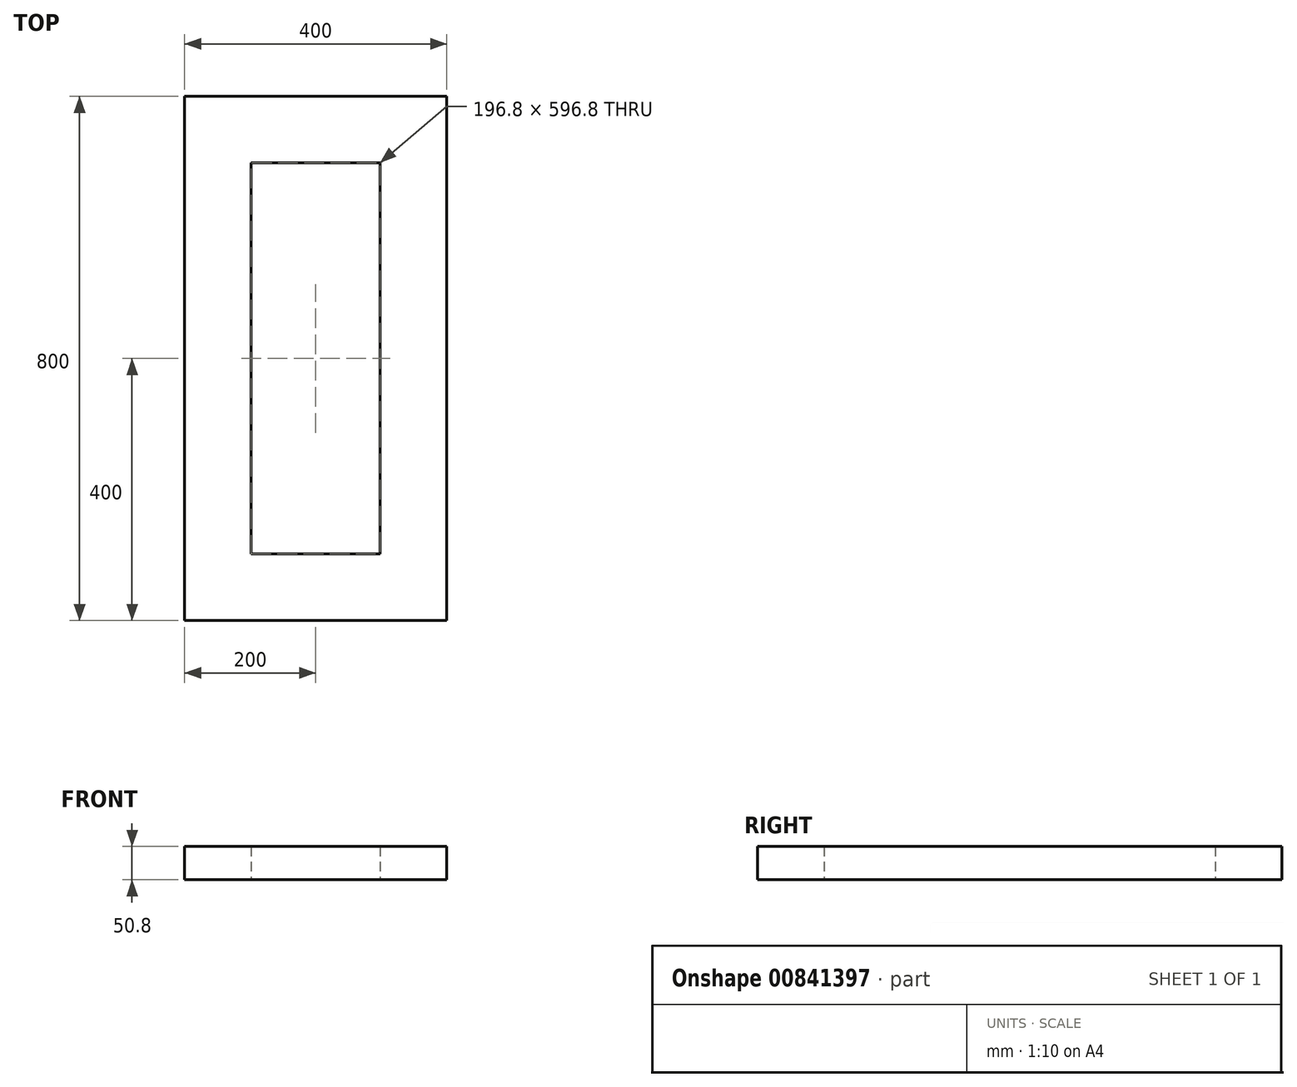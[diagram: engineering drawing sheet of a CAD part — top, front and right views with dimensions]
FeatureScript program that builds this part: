
annotation { "Feature Type Name" : "Feature", "Feature Type Description" : "" }
export const myFeature = defineFeature(function(context is Context, id is Id, definition is map)
    precondition{}
    {
        {
            var Q0;
            Q0=qCreatedBy(makeId("Top.planeOp"),FACE);
            var sketch = newSketch(context, id + "F0", { "sketchPlane" : qUnion([Q0])});
            skLineSegment(sketch, "E0.bottom", {"start": v(0, 0) * mm, "end": v(400, 0) * mm});
            skLineSegment(sketch, "E0.top", {"start": v(0, -800) * mm, "end": v(400, -800) * mm});
            skLineSegment(sketch, "E0.left", {"start": v(0, 0) * mm, "end": v(0, -800) * mm});
            skLineSegment(sketch, "E0.right", {"start": v(400, 0) * mm, "end": v(400, -800) * mm});
            skLineSegment(sketch, "E1.bottom", {"start": v(101.6, -101.6) * mm, "end": v(298.4, -101.6) * mm});
            skLineSegment(sketch, "E1.top", {"start": v(101.6, -698.4) * mm, "end": v(298.4, -698.4) * mm});
            skLineSegment(sketch, "E1.left", {"start": v(101.6, -101.6) * mm, "end": v(101.6, -698.4) * mm});
            skLineSegment(sketch, "E1.right", {"start": v(298.4, -101.6) * mm, "end": v(298.4, -698.4) * mm});
            skSolve(sketch);
        }
        {
            var Q0;
            Q0=makeQuery(id+"F0.imprint","IMPRINT",FACE,{"disambiguationData":[TD([[makeQuery(id+"F0.imprint","IMPRINT",EDGE,{"derivedFrom":sQuery(id+"F0.wireOp",EDGE,"E0.bottom")}),-1.0]])]});
            extrude(context, id + "F1", {"entities" : qUnion([Q0]), "depth" : 50.8 * mm, "offsetDistance" : 25 * mm});
        }
    });
